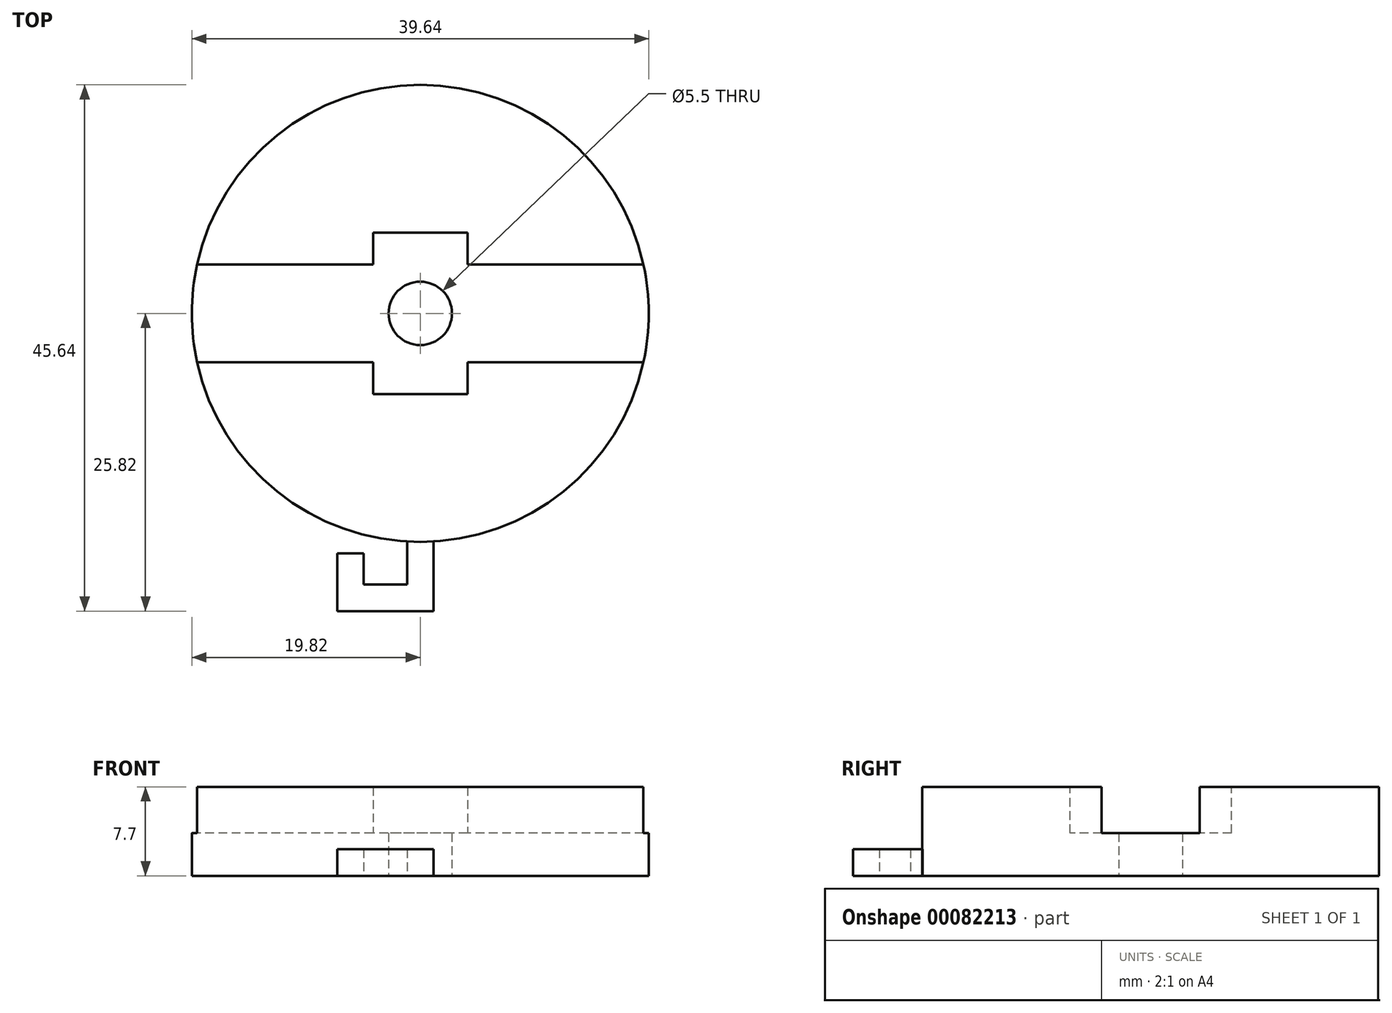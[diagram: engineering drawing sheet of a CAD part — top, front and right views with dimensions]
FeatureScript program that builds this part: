
annotation { "Feature Type Name" : "Feature", "Feature Type Description" : "" }
export const myFeature = defineFeature(function(context is Context, id is Id, definition is map)
    precondition{}
    {
        {
            var Q0;
            Q0=qCreatedBy(makeId("Top.planeOp"),FACE);
            var sketch = newSketch(context, id + "F0", { "sketchPlane" : qUnion([Q0])});
            skCircle(sketch, "E0", {"center": v(0, 0) * mm, "radius": 19.82 * mm});
            skSolve(sketch);
        }
        {
            var Q0;
            Q0=qSketchRegion(id+"F0",true);
            extrude(context, id + "F1", {"entities" : qUnion([Q0]), "depth" : 7.7 * mm});
        }
        {
            var Q0;
            Q0=makeQuery(id+"F1.opExtrude","CAP_FACE",FACE,{"disambiguationData":[OSD([sQuery(id+"F0.wireOp",EDGE,"E0")])],"isStart":false});
            var sketch = newSketch(context, id + "F2", { "sketchPlane" : qUnion([Q0])});
            skLineSegment(sketch, "E1.bottom", {"start": v(4.1, 7) * mm, "end": v(-4.1, 7) * mm});
            skLineSegment(sketch, "E1.top", {"start": v(4.1, -7) * mm, "end": v(-4.1, -7) * mm});
            skLineSegment(sketch, "E1.left", {"start": v(4.1, 7) * mm, "end": v(4.1, -7) * mm});
            skLineSegment(sketch, "E1.right", {"start": v(-4.1, 7) * mm, "end": v(-4.1, -7) * mm});
            skPoint(sketch, "E1.middle", {"position": v(0, 0) * mm});
            skSolve(sketch);
        }
        {
            var Q0;
            Q0=qSketchRegion(id+"F2",true);
            extrude(context, id + "F3", {"entities" : qUnion([Q0]), "operationType" : NewBodyOperationType.REMOVE, "oppositeDirection" : true, "depth" : 4 * mm});
        }
        {
            var Q0;
            Q0=makeQuery(id+"F1.opExtrude","CAP_FACE",FACE,{"disambiguationData":[OSD([sQuery(id+"F0.wireOp",EDGE,"E0")])],"isStart":false});
            var sketch = newSketch(context, id + "F4", { "sketchPlane" : qUnion([Q0])});
            skLineSegment(sketch, "E2.bottom", {"start": v(20.32, -4.25) * mm, "end": v(-20.32, -4.25) * mm});
            skLineSegment(sketch, "E2.top", {"start": v(20.32, 4.25) * mm, "end": v(-20.32, 4.25) * mm});
            skLineSegment(sketch, "E2.left", {"start": v(20.32, -4.25) * mm, "end": v(20.32, 4.25) * mm});
            skLineSegment(sketch, "E2.right", {"start": v(-20.32, -4.25) * mm, "end": v(-20.32, 4.25) * mm});
            skPoint(sketch, "E2.middle", {"position": v(0, 0) * mm});
            skSolve(sketch);
        }
        {
            var Q0;
            Q0=qSketchRegion(id+"F4",true);
            extrude(context, id + "F5", {"entities" : qUnion([Q0]), "operationType" : NewBodyOperationType.REMOVE, "oppositeDirection" : true, "depth" : 4 * mm});
        }
        {
            var Q0;
            Q0=makeQuery(id+"F1.opExtrude","CAP_FACE",FACE,{"disambiguationData":[OSD([sQuery(id+"F0.wireOp",EDGE,"E0")])],"isStart":true});
            var sketch = newSketch(context, id + "F6", { "sketchPlane" : qUnion([Q0])});
            skLineSegment(sketch, "E3.bottom", {"start": v(1.15, 25.82) * mm, "end": v(-1.15, 25.82) * mm});
            skLineSegment(sketch, "E3.left", {"start": v(1.15, 19.82) * mm, "end": v(1.15, 25.82) * mm});
            skLineSegment(sketch, "E3.right", {"start": v(-1.15, 19.82) * mm, "end": v(-1.15, 25.82) * mm});
            skPoint(sketch, "E3.middle", {"position": v(0, 22.82) * mm});
            skLineSegment(sketch, "E4.bottom", {"start": v(1.15, 25.82) * mm, "end": v(-7.2, 25.82) * mm});
            skLineSegment(sketch, "E4.top", {"start": v(1.15, 23.52) * mm, "end": v(-7.2, 23.52) * mm});
            skLineSegment(sketch, "E4.left", {"start": v(1.15, 25.82) * mm, "end": v(1.15, 23.52) * mm});
            skLineSegment(sketch, "E4.right", {"start": v(-7.2, 25.82) * mm, "end": v(-7.2, 23.52) * mm});
            skLineSegment(sketch, "E5.bottom", {"start": v(-7.2, 25.82) * mm, "end": v(-4.9, 25.82) * mm});
            skLineSegment(sketch, "E5.top", {"start": v(-7.2, 20.82) * mm, "end": v(-4.9, 20.82) * mm});
            skLineSegment(sketch, "E5.left", {"start": v(-7.2, 25.82) * mm, "end": v(-7.2, 20.82) * mm});
            skLineSegment(sketch, "E5.right", {"start": v(-4.9, 25.82) * mm, "end": v(-4.9, 20.82) * mm});
            skLineSegment(sketch, "E6", {"start": v(-1.15, 19.82) * mm, "end": v(-1.15, 19.52) * mm});
            skLineSegment(sketch, "E7", {"start": v(-1.15, 19.52) * mm, "end": v(1.17, 19.55) * mm});
            skLineSegment(sketch, "E8", {"start": v(1.17, 19.55) * mm, "end": v(1.15, 19.82) * mm});
            skSolve(sketch);
        }
        {
            var Q0;
            Q0=qSketchRegion(id+"F6",true);
            extrude(context, id + "F7", {"entities" : qUnion([Q0]), "operationType" : NewBodyOperationType.ADD, "oppositeDirection" : true, "depth" : 2.3 * mm});
        }
        {
            var Q0;
            Q0=makeQuery(id+"F7.boolean.opBoolean","MERGE",FACE,{"derivedFrom":[makeQuery(id+"F1.opExtrude","CAP_FACE",FACE,{"disambiguationData":[OSD([sQuery(id+"F0.wireOp",EDGE,"E0")])],"isStart":true}),makeQuery(id+"F7.opExtrude","CAP_FACE",FACE,{"disambiguationData":[OSD([sQuery(id+"F6.wireOp",EDGE,"E3.left"),sQuery(id+"F6.wireOp",EDGE,"E3.right"),sQuery(id+"F6.wireOp",EDGE,"E4.bottom"),sQuery(id+"F6.wireOp",EDGE,"E4.top"),sQuery(id+"F6.wireOp",EDGE,"E4.left"),sQuery(id+"F6.wireOp",EDGE,"E5.bottom"),sQuery(id+"F6.wireOp",EDGE,"E5.top"),sQuery(id+"F6.wireOp",EDGE,"E5.left"),sQuery(id+"F6.wireOp",EDGE,"E5.right"),sQuery(id+"F6.wireOp",EDGE,"E6"),sQuery(id+"F6.wireOp",EDGE,"E7"),sQuery(id+"F6.wireOp",EDGE,"E8")])],"isStart":true})]});
            var sketch = newSketch(context, id + "F8", { "sketchPlane" : qUnion([Q0])});
            skCircle(sketch, "E9", {"center": v(0, 0) * mm, "radius": 2.75 * mm});
            skSolve(sketch);
        }
        {
            var Q0;
            Q0=qSketchRegion(id+"F8",true);
            extrude(context, id + "F9", {"entities" : qUnion([Q0]), "operationType" : NewBodyOperationType.REMOVE, "oppositeDirection" : true, "depth" : 25 * mm});
        }
    });
